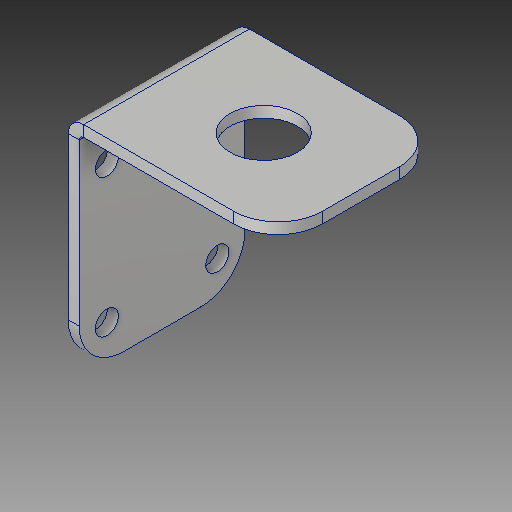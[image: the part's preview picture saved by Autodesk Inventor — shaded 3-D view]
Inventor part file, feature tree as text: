
AUTODESK INVENTOR PART (.ipt)
format: ipt  version: 2019 (Build 230136000, 136)  size: 137,216 bytes
history: native  units: mm
features: other x3, sketch x3
ambient origin geometry x8: Origin, YZ Plane, XZ Plane, XY Plane, X Axis, Y Axis, Z Axis, Center Point
bodies: Solid1 (feature_tree)
feature tree (6):
  other  "Hot End Mount.ipt"
  other  "Solid2::Hot End Mount.ipt"
  other  "TaggingFeature1"
  sketch  "Sketch1"  dims[d0=10.0mm]
  sketch  "Sketch2"
  sketch  "Sketch3"
